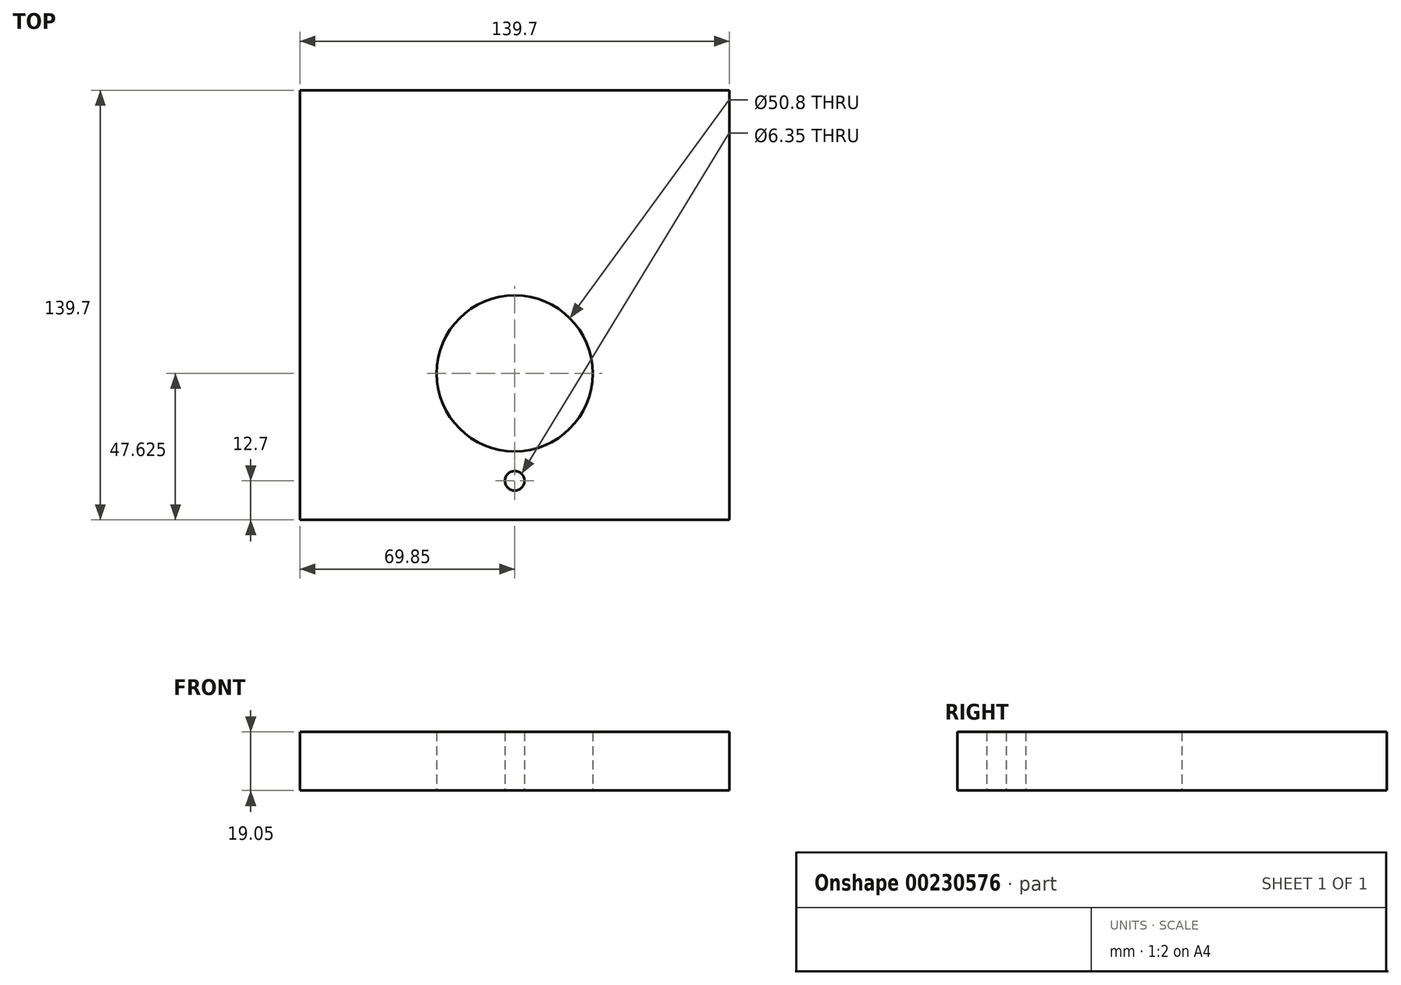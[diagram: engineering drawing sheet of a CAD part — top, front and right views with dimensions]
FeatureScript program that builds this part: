
annotation { "Feature Type Name" : "Feature", "Feature Type Description" : "" }
export const myFeature = defineFeature(function(context is Context, id is Id, definition is map)
    precondition{}
    {
        {
            var Q0;
            Q0=qCreatedBy(makeId("Top.planeOp"),FACE);
            var sketch = newSketch(context, id + "F0", { "sketchPlane" : qUnion([Q0])});
            skLineSegment(sketch, "E0.bottom", {"start": v(-69.85, -69.85) * mm, "end": v(69.85, -69.85) * mm});
            skLineSegment(sketch, "E0.top", {"start": v(-69.85, 69.85) * mm, "end": v(69.85, 69.85) * mm});
            skLineSegment(sketch, "E0.left", {"start": v(-69.85, -69.85) * mm, "end": v(-69.85, 69.85) * mm});
            skLineSegment(sketch, "E0.right", {"start": v(69.85, -69.85) * mm, "end": v(69.85, 69.85) * mm});
            skPoint(sketch, "E0.middle", {"position": v(0, 0) * mm});
            skLineSegment(sketch, "E1", {"start": v(0, -69.85) * mm, "end": v(0, -57.15) * mm});
            skPoint(sketch, "E1.endSnap0", {"position": v(0, -69.85) * mm});
            skCircle(sketch, "E2", {"center": v(0, -22.22) * mm, "radius": 25.4 * mm});
            skCircle(sketch, "E3", {"center": v(0, -57.15) * mm, "radius": 3.18 * mm});
            skSolve(sketch);
        }
        {
            var Q0;
            Q0 = qSketchRegion(id + "F0", true);
            extrude(context, id + "F1", {"entities" : qUnion([Q0]), "depth" : 19.05 * mm});
        }
    });
